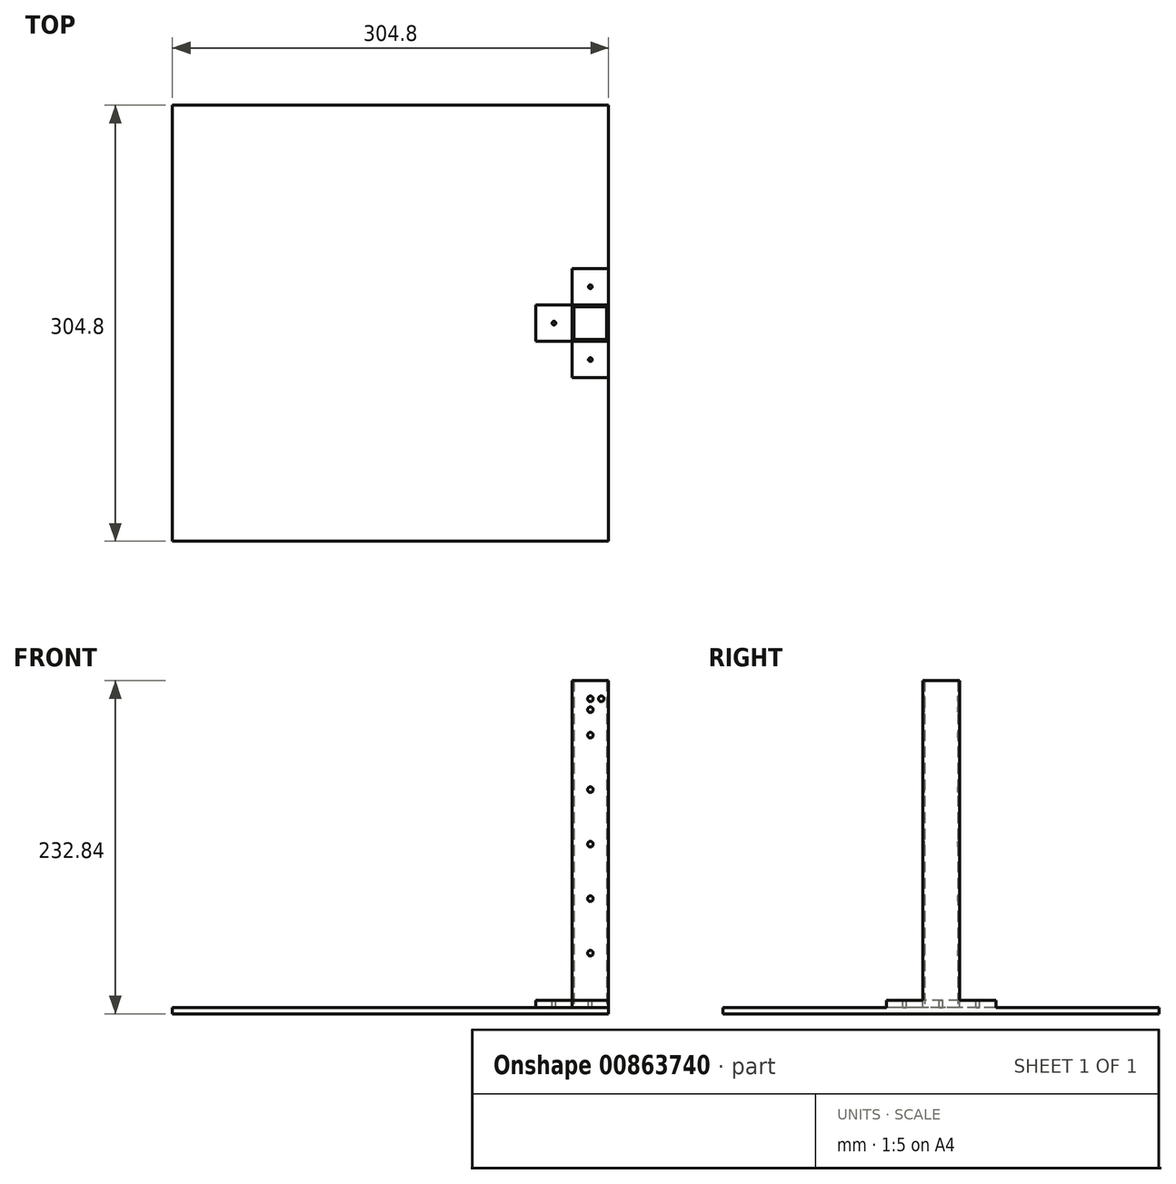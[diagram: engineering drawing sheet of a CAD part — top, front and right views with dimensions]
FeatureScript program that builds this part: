
annotation { "Feature Type Name" : "Feature", "Feature Type Description" : "" }
export const myFeature = defineFeature(function(context is Context, id is Id, definition is map)
    precondition{}
    {
        {
            var Q0;
            Q0=qCreatedBy(makeId("Top.planeOp"),FACE);
            var sketch = newSketch(context, id + "F0", { "sketchPlane" : qUnion([Q0])});
            skLineSegment(sketch, "E0.bottom", {"start": v(152.4, 152.4) * mm, "end": v(-152.4, 152.4) * mm});
            skLineSegment(sketch, "E0.top", {"start": v(152.4, -152.4) * mm, "end": v(-152.4, -152.4) * mm});
            skLineSegment(sketch, "E0.left", {"start": v(152.4, 152.4) * mm, "end": v(152.4, -152.4) * mm});
            skLineSegment(sketch, "E0.right", {"start": v(-152.4, 152.4) * mm, "end": v(-152.4, -152.4) * mm});
            skPoint(sketch, "E0.middle", {"position": v(0, 0) * mm});
            skSolve(sketch);
        }
        {
            var Q0;
            Q0 = qSketchRegion(id + "F0", true);
            extrude(context, id + "F1", {"entities" : qUnion([Q0]), "depth" : 4.24 * mm, "offsetDistance" : 25.4 * mm});
        }
        {
            var Q0;
            Q0=makeQuery(id+"F1.opExtrude","CAP_FACE",FACE,{"disambiguationData":[OSD([sQuery(id+"F0.wireOp",EDGE,"E0.bottom"),sQuery(id+"F0.wireOp",EDGE,"E0.top"),sQuery(id+"F0.wireOp",EDGE,"E0.left"),sQuery(id+"F0.wireOp",EDGE,"E0.right")])],"isStart":false});
            var sketch = newSketch(context, id + "F2", { "sketchPlane" : qUnion([Q0])});
            skLineSegment(sketch, "E1.bottom", {"start": v(152.4, 12.76) * mm, "end": v(126.87, 12.76) * mm});
            skLineSegment(sketch, "E1.top", {"start": v(152.4, -12.76) * mm, "end": v(126.87, -12.76) * mm});
            skLineSegment(sketch, "E1.left", {"start": v(152.4, 12.76) * mm, "end": v(152.4, -12.76) * mm});
            skLineSegment(sketch, "E1.right", {"start": v(126.87, 12.76) * mm, "end": v(126.87, -12.76) * mm});
            skPoint(sketch, "E1.middle", {"position": v(139.64, 0) * mm});
            skLineSegment(sketch, "E2.bottom", {"start": v(151.13, 11.5) * mm, "end": v(128.14, 11.5) * mm});
            skLineSegment(sketch, "E2.top", {"start": v(151.13, -11.5) * mm, "end": v(128.14, -11.5) * mm});
            skLineSegment(sketch, "E2.left", {"start": v(151.13, 11.5) * mm, "end": v(151.13, -11.5) * mm});
            skLineSegment(sketch, "E2.right", {"start": v(128.14, 11.5) * mm, "end": v(128.14, -11.5) * mm});
            skSolve(sketch);
        }
        {
            var Q0;
            Q0 = qSketchRegion(id + "F2", true);
            extrude(context, id + "F3", {"entities" : qUnion([Q0]), "operationType" : NewBodyOperationType.ADD, "depth" : 228.6 * mm, "offsetDistance" : 25.4 * mm});
        }
        {
            var Q0;
            Q0=makeQuery(id+"F3.opExtrude","SWEPT_FACE",FACE,{"disambiguationData":[OSD([sQuery(id+"F2.wireOp",EDGE,"E1.top")])]});
            var sketch = newSketch(context, id + "F4", { "sketchPlane" : qUnion([Q0])});
            skCircle(sketch, "E3", {"center": v(139.64, 42.34) * mm, "radius": 1.9 * mm});
            skPoint(sketch, "E3.centerSnap0", {"position": v(139.64, 4.24) * mm});
            skCircle(sketch, "E4.0.1.0", {"center": v(139.64, 80.44) * mm, "radius": 1.9 * mm});
            skCircle(sketch, "E4.0.2.0", {"center": v(139.64, 118.54) * mm, "radius": 1.9 * mm});
            skCircle(sketch, "E4.0.3.0", {"center": v(139.64, 156.64) * mm, "radius": 1.9 * mm});
            skCircle(sketch, "E4.0.4.0", {"center": v(139.64, 194.74) * mm, "radius": 1.9 * mm});
            skLineSegment(sketch, "E4.direction1", {"start": v(139.64, 42.34) * mm, "end": v(165.04, 42.34) * mm, "construction": true});
            skLineSegment(sketch, "E4.direction2", {"start": v(139.64, 42.34) * mm, "end": v(139.64, 80.44) * mm, "construction": true});
            skSolve(sketch);
        }
        {
            var Q0;
            Q0 = qSketchRegion(id + "F4", true);
            extrude(context, id + "F5", {"entities" : qUnion([Q0]), "operationType" : NewBodyOperationType.REMOVE, "endBound" : BoundingType.THROUGH_ALL, "oppositeDirection" : true, "depth" : 25.4 * mm, "offsetDistance" : 25.4 * mm});
        }
        {
            var Q0;
            Q0=makeQuery(id+"F3.opExtrude","SWEPT_FACE",FACE,{"disambiguationData":[OSD([sQuery(id+"F2.wireOp",EDGE,"E1.top")])]});
            var sketch = newSketch(context, id + "F6", { "sketchPlane" : qUnion([Q0])});
            skLineSegment(sketch, "E5.bottom", {"start": v(126.87, 4.24) * mm, "end": v(152.4, 4.24) * mm});
            skLineSegment(sketch, "E5.top", {"start": v(126.87, 9.32) * mm, "end": v(152.4, 9.32) * mm});
            skLineSegment(sketch, "E5.left", {"start": v(126.87, 4.24) * mm, "end": v(126.87, 9.32) * mm});
            skLineSegment(sketch, "E5.right", {"start": v(152.4, 4.24) * mm, "end": v(152.4, 9.32) * mm});
            skSolve(sketch);
        }
        {
            var Q0;
            Q0 = qSketchRegion(id + "F6", true);
            extrude(context, id + "F7", {"entities" : qUnion([Q0]), "operationType" : NewBodyOperationType.ADD, "depth" : 25.4 * mm, "offsetDistance" : 25.4 * mm});
        }
        {
            var Q0;
            Q0=makeQuery(id+"F7.opExtrude","SWEPT_FACE",FACE,{"disambiguationData":[OSD([sQuery(id+"F6.wireOp",EDGE,"E5.top")])]});
            var sketch = newSketch(context, id + "F8", { "sketchPlane" : qUnion([Q0])});
            skCircle(sketch, "E6", {"center": v(139.64, -25.46) * mm, "radius": 1.27 * mm});
            skPoint(sketch, "E6.centerSnap0", {"position": v(152.4, -25.46) * mm});
            skPoint(sketch, "E6.centerSnap1", {"position": v(139.64, -38.16) * mm});
            skSolve(sketch);
        }
        {
            var Q0;
            Q0 = qSketchRegion(id + "F8", true);
            extrude(context, id + "F9", {"entities" : qUnion([Q0]), "operationType" : NewBodyOperationType.REMOVE, "oppositeDirection" : true, "depth" : 5.08 * mm, "offsetDistance" : 25.4 * mm});
        }
        {
            var Q0;
            Q0=makeQuery(id+"F1.opExtrude","SWEPT_BODY",BODY,{"disambiguationData":[OSD([sQuery(id+"F0.wireOp",EDGE,"E0.bottom"),sQuery(id+"F0.wireOp",EDGE,"E0.top"),sQuery(id+"F0.wireOp",EDGE,"E0.left"),sQuery(id+"F0.wireOp",EDGE,"E0.right")])]});
            var Q1;
            Q1=qCreatedBy(makeId("Front.planeOp"),FACE);
            mirror(context, id + "F10", {"operationType" : NewBodyOperationType.ADD, "entities" : qUnion([Q0]), "mirrorPlane" : qUnion([Q1])});
        }
        {
            var Q0;
            {var subQ0=makeQuery(id+"F7.boolean.opBoolean","MERGE",FACE,{"derivedFrom":[makeQuery(id+"F3.opExtrude","SWEPT_FACE",FACE,{"disambiguationData":[OSD([sQuery(id+"F2.wireOp",EDGE,"E1.right")])]}),makeQuery(id+"F7.opExtrude","SWEPT_FACE",FACE,{"disambiguationData":[OSD([sQuery(id+"F6.wireOp",EDGE,"E5.left")])]})]});Q0=makeQuery(id+"F10.boolean.opBoolean","MERGE",FACE,{"derivedFrom":[subQ0,makeQuery(id+"F10.opPattern","COPY",FACE,{"derivedFrom":subQ0,"instanceName":"1"})]});}
            var sketch = newSketch(context, id + "F11", { "sketchPlane" : qUnion([Q0])});
            skLineSegment(sketch, "E7.bottom", {"start": v(-12.76, 4.24) * mm, "end": v(12.76, 4.24) * mm});
            skLineSegment(sketch, "E7.top", {"start": v(-12.76, 9.32) * mm, "end": v(12.76, 9.32) * mm});
            skLineSegment(sketch, "E7.left", {"start": v(-12.76, 4.24) * mm, "end": v(-12.76, 9.32) * mm});
            skLineSegment(sketch, "E7.right", {"start": v(12.76, 4.24) * mm, "end": v(12.76, 9.32) * mm});
            skSolve(sketch);
        }
        {
            var Q0;
            Q0 = qSketchRegion(id + "F11", true);
            extrude(context, id + "F12", {"entities" : qUnion([Q0]), "operationType" : NewBodyOperationType.ADD, "depth" : 25.4 * mm, "offsetDistance" : 25.4 * mm});
        }
        {
            var Q0;
            Q0=makeQuery(id+"F12.opExtrude","SWEPT_FACE",FACE,{"disambiguationData":[OSD([sQuery(id+"F11.wireOp",EDGE,"E7.top")])]});
            var sketch = newSketch(context, id + "F13", { "sketchPlane" : qUnion([Q0])});
            skCircle(sketch, "E8", {"center": v(114.17, 0) * mm, "radius": 1.27 * mm});
            skPoint(sketch, "E8.centerSnap0", {"position": v(114.17, -12.76) * mm});
            skSolve(sketch);
        }
        {
            var Q0;
            Q0 = qSketchRegion(id + "F13", true);
            extrude(context, id + "F14", {"entities" : qUnion([Q0]), "operationType" : NewBodyOperationType.REMOVE, "oppositeDirection" : true, "depth" : 5.08 * mm, "offsetDistance" : 25.4 * mm});
        }
        {
            var Q0;
            Q0=makeQuery(id+"F3.opExtrude","SWEPT_FACE",FACE,{"disambiguationData":[OSD([sQuery(id+"F2.wireOp",EDGE,"E1.top")])]});
            var sketch = newSketch(context, id + "F15", { "sketchPlane" : qUnion([Q0])});
            skCircle(sketch, "E9", {"center": v(139.64, 220.14) * mm, "radius": 1.9 * mm});
            skCircle(sketch, "E10", {"center": v(147.26, 220.14) * mm, "radius": 1.9 * mm});
            skCircle(sketch, "E11", {"center": v(139.64, 212.52) * mm, "radius": 1.9 * mm});
            skSolve(sketch);
        }
        {
            var Q0;
            Q0 = qSketchRegion(id + "F15", true);
            extrude(context, id + "F16", {"entities" : qUnion([Q0]), "operationType" : NewBodyOperationType.REMOVE, "endBound" : BoundingType.THROUGH_ALL, "oppositeDirection" : true, "depth" : 25.4 * mm, "offsetDistance" : 25.4 * mm});
        }
    });
